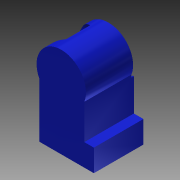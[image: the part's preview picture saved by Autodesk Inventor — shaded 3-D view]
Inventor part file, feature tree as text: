
AUTODESK INVENTOR PART (.ipt)
format: ipt  version: 2015 (Build 190159000, 159)  size: 148,480 bytes
history: native  units: mm
features: extrude x5, sketch x5, fillet x1
ambient origin geometry x8: Origin, YZ Plane, XZ Plane, XY Plane, X Axis, Y Axis, Z Axis, Center Point
bodies: Solid1 (feature_tree)
feature tree (11):
  extrude  "Extrusion1"  Depth=7.83mm
  extrude  "Extrusion2"  Depth=3.54mm
  extrude  "Extrusion3"  Depth=6.457mm
  extrude  "Extrusion4"  Depth=7.108mm
  extrude  "Extrusion5"  Depth=2.0mm TaperAngle=0.0deg
  fillet  "Fillet1"  Radius=5.0mm
  sketch  "Sketch1"  dims[d0=7.83mm d1=9.45mm]
  sketch  "Sketch2"  dims[d2=3.54mm d3=3.154mm]
  sketch  "Sketch3"  dims[d4=3.171mm d5=6.457mm]
  sketch  "Sketch4"  dims[d6=7.108mm d7=0.0mm d8=5.0mm]
  sketch  "Sketch5"  dims[d9=3.2mm d10=2.0mm d11=0.0mm d12=5.0mm d13=3.0mm d14=2.0mm d15=0.0mm d16=8.0mm d17=2.0mm d18=0.0mm d19=0.345mm d20=0.0mm d21=0.1mm]
